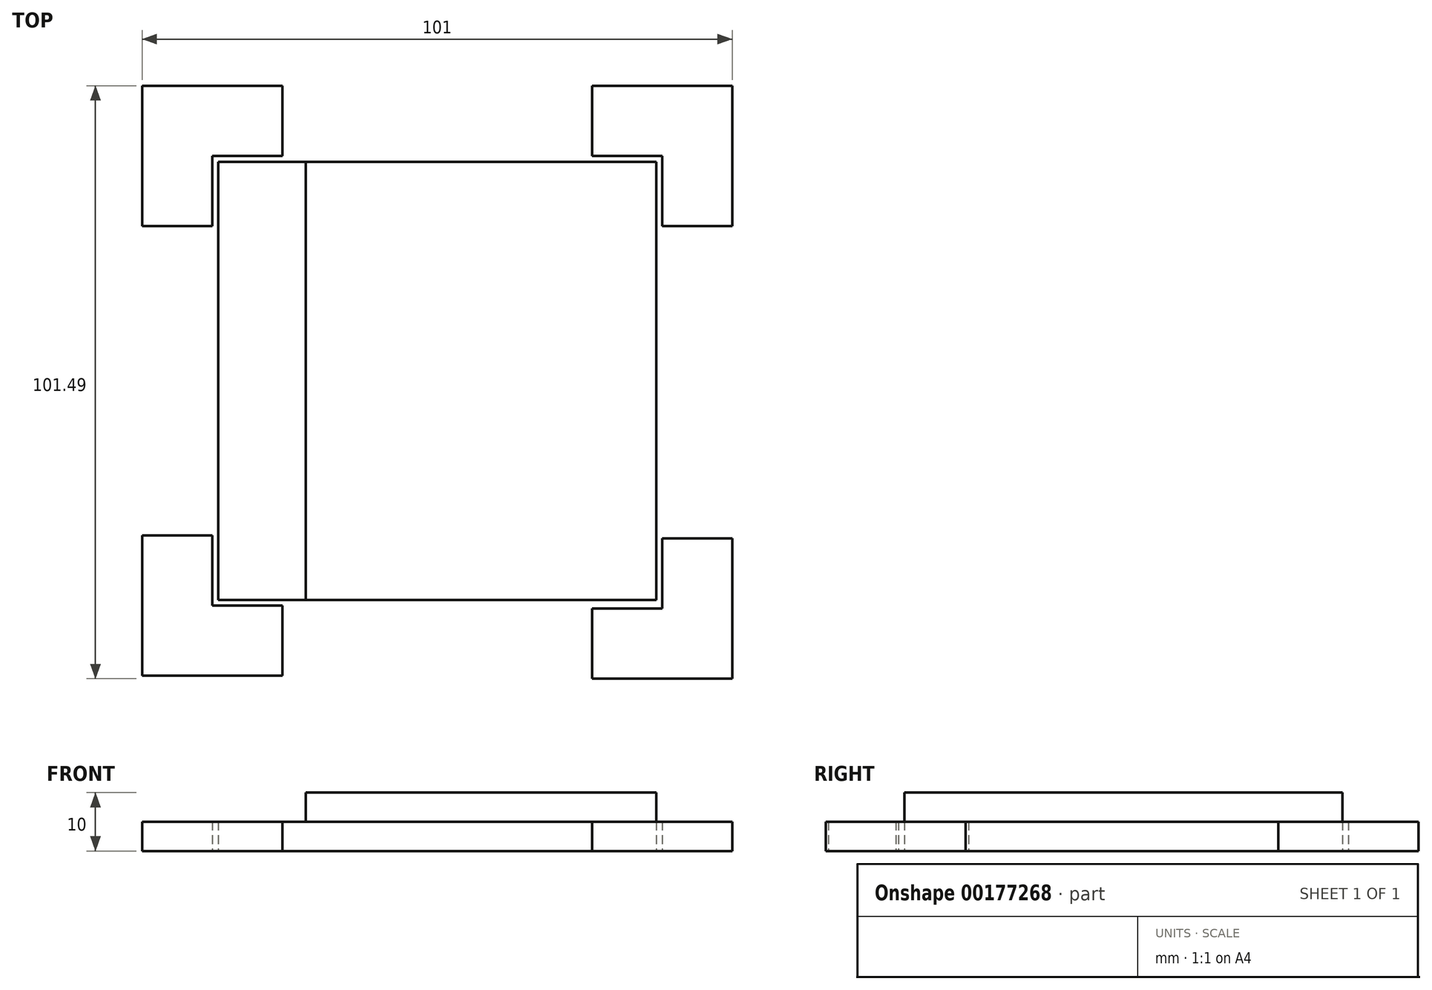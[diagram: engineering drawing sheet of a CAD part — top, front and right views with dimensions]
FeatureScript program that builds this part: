
annotation { "Feature Type Name" : "Feature", "Feature Type Description" : "" }
export const myFeature = defineFeature(function(context is Context, id is Id, definition is map)
    precondition{}
    {
        {
            var Q0;
            Q0=qCreatedBy(makeId("Top.planeOp"),FACE);
            var sketch = newSketch(context, id + "F0", { "sketchPlane" : qUnion([Q0])});
            skLineSegment(sketch, "E0.bottom", {"start": v(0, 0) * mm, "end": v(75, 0) * mm});
            skLineSegment(sketch, "E0.top", {"start": v(0, -75) * mm, "end": v(75, -75) * mm});
            skLineSegment(sketch, "E0.left", {"start": v(0, 0) * mm, "end": v(0, -75) * mm});
            skLineSegment(sketch, "E0.right", {"start": v(75, 0) * mm, "end": v(75, -75) * mm});
            skLineSegment(sketch, "E1", {"start": v(64, 1) * mm, "end": v(76, 1) * mm});
            skLineSegment(sketch, "E2", {"start": v(76, 1) * mm, "end": v(76, -11) * mm});
            skLineSegment(sketch, "E3", {"start": v(76, -11) * mm, "end": v(88, -11) * mm});
            skLineSegment(sketch, "E4", {"start": v(88, -11) * mm, "end": v(88, 13) * mm});
            skLineSegment(sketch, "E5", {"start": v(88, 13) * mm, "end": v(64, 13) * mm});
            skLineSegment(sketch, "E6", {"start": v(64, 13) * mm, "end": v(64, 1) * mm});
            skLineSegment(sketch, "E7", {"start": v(-1, -64) * mm, "end": v(-1, -76) * mm});
            skLineSegment(sketch, "E8", {"start": v(-1, -76) * mm, "end": v(11, -76) * mm});
            skLineSegment(sketch, "E9", {"start": v(11, -76) * mm, "end": v(11, -88) * mm});
            skLineSegment(sketch, "E10", {"start": v(11, -88) * mm, "end": v(-13, -88) * mm});
            skLineSegment(sketch, "E11", {"start": v(-13, -88) * mm, "end": v(-13, -64) * mm});
            skLineSegment(sketch, "E12", {"start": v(-13, -64) * mm, "end": v(-1, -64) * mm});
            skLineSegment(sketch, "E13", {"start": v(-1, 1) * mm, "end": v(11, 1) * mm});
            skLineSegment(sketch, "E14", {"start": v(11, 1) * mm, "end": v(11, 13) * mm});
            skLineSegment(sketch, "E15", {"start": v(11, 13) * mm, "end": v(-13, 13) * mm});
            skLineSegment(sketch, "E16", {"start": v(-13, 13) * mm, "end": v(-13, -11) * mm});
            skLineSegment(sketch, "E17", {"start": v(-13, -11) * mm, "end": v(-1, -11) * mm});
            skLineSegment(sketch, "E18", {"start": v(-1, -11) * mm, "end": v(-1, 1) * mm});
            skLineSegment(sketch, "E19", {"start": v(76, -76.5) * mm, "end": v(76, -64.5) * mm});
            skLineSegment(sketch, "E20", {"start": v(76, -64.5) * mm, "end": v(88, -64.5) * mm});
            skLineSegment(sketch, "E21", {"start": v(88, -64.5) * mm, "end": v(88, -88.5) * mm});
            skLineSegment(sketch, "E22", {"start": v(88, -88.5) * mm, "end": v(64, -88.5) * mm});
            skLineSegment(sketch, "E23", {"start": v(64, -88.5) * mm, "end": v(64, -76.5) * mm});
            skLineSegment(sketch, "E24", {"start": v(64, -76.5) * mm, "end": v(76, -76.5) * mm});
            skSolve(sketch);
        }
        {
            var Q0;
            Q0 = qSketchRegion(id + "F0", true);
            extrude(context, id + "F1", {"entities" : qUnion([Q0]), "depth" : 5 * mm});
        }
        {
            var Q0;
            Q0=makeQuery(id+"F1.opExtrude","CAP_FACE",FACE,{"disambiguationData":[OSD([sQuery(id+"F0.wireOp",EDGE,"E0.bottom"),sQuery(id+"F0.wireOp",EDGE,"E0.top"),sQuery(id+"F0.wireOp",EDGE,"E0.left"),sQuery(id+"F0.wireOp",EDGE,"E0.right")])],"isStart":false});
            var sketch = newSketch(context, id + "F2", { "sketchPlane" : qUnion([Q0])});
            skLineSegment(sketch, "E25.bottom", {"start": v(15, 0) * mm, "end": v(75, 0) * mm});
            skLineSegment(sketch, "E25.top", {"start": v(15, -75) * mm, "end": v(75, -75) * mm});
            skLineSegment(sketch, "E25.left", {"start": v(15, 0) * mm, "end": v(15, -75) * mm});
            skLineSegment(sketch, "E25.right", {"start": v(75, 0) * mm, "end": v(75, -75) * mm});
            skSolve(sketch);
        }
        {
            var Q0;
            Q0 = qSketchRegion(id + "F2", true);
            extrude(context, id + "F3", {"entities" : qUnion([Q0]), "depth" : 5 * mm});
        }
    });
